# Revit family: Power-ModularDevices-GEWISS-90AM-SPD_TYPE1+2_1PN_12kA
name_source: partatom
category: Apparecchi elettrici
revit_build: Autodesk Revit 2016 (Build: 20161004_0715(x64)
units: mm (PartAtom-declared; Revit-internal decimal feet)

## family parameters
Condiviso = No
Host = Superficie
Mantenere orientamento annotazione = Sì
Numero OmniClass = 23.80.50.00
Punto di calcolo locali = Sì
Quota connettore circolare = Usa diametro
Taglio con vuoti quando caricato = No
Tipo di parte = Normale
Titolo OmniClass = Terminals for Power Supply

## types (1)
- Power-ModularDevices-GEWISS-90AM-SPD_TYPE1+2_1PN_12kA
    Barra_DIN = 0 mm  [stored 0 ft]
    Catalogue = POWER
    Catalogue Range = 90 AM
    Descrizione = LST - SPD 1P+N 12,5KA T1+2
    EAN code = 8011564801998
    Electrocod = 0641
    IDF = a3027289-0c26-4ed6-b6f9-3071d9977e8a
    IDT = 3eadec53-785f-4656-9471-459a1ac69818
    Immagine tipo = GWD6401.jpg
    Impulse current: = 12,5KA
    Maximum discharge current: = 65KA
    Modello = GWD6401
    No. Chorus modules = 2
    No. of modules EN 50022 = 2
    No. of poles = 1P+N
    Number of poles = 1P+N
    Numero di poli = 1
    Produttore = GEWISS S.p.A.
    Prospetto di default = 1219 mm
    Rated voltage = 230Vac
    Rated voltage AC = 230V
    SEO = Limiter
    Simbolo in pianta = Sì
    Spostamento_x = -50 mm
    Technical sheet = https://www.gewiss.com
    Type = 1+2
    Type: = 1+2
    URL = https://www.gewiss.com
    Version file RFA = 18.0
    carico = Altro
    potenza in watt = 0 V

note: [stored X ft] marks values corroborated as IEEE doubles in the binary element streams (Revit-internal decimal feet)
